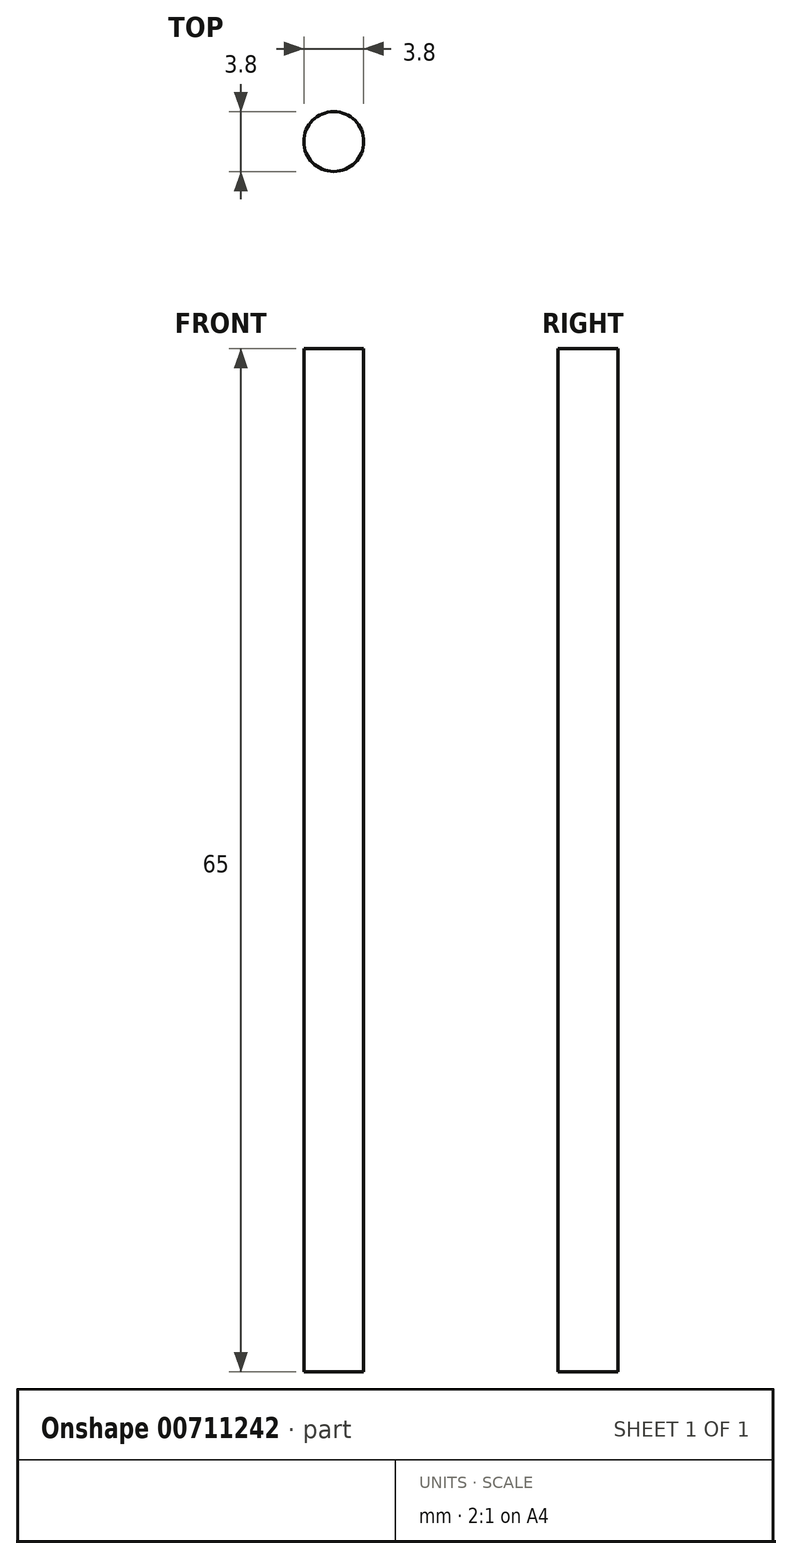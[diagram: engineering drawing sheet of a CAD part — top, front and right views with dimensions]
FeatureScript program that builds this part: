
annotation { "Feature Type Name" : "Feature", "Feature Type Description" : "" }
export const myFeature = defineFeature(function(context is Context, id is Id, definition is map)
    precondition{}
    {
        {
            var Q0;
            Q0=qCreatedBy(makeId("Top.planeOp"),FACE);
            var sketch = newSketch(context, id + "F0", { "sketchPlane" : qUnion([Q0])});
            skCircle(sketch, "E0", {"center": v(0, 0) * mm, "radius": 1.9 * mm});
            skSolve(sketch);
        }
        {
            var Q0;
            Q0=makeQuery(id+"F0.imprint","IMPRINT",FACE,{"disambiguationData":[TD([[makeQuery(id+"F0.imprint","IMPRINT",EDGE,{"derivedFrom":sQuery(id+"F0.wireOp",EDGE,"E0")}),1.0]])]});
            extrude(context, id + "F1", {"entities" : qUnion([Q0]), "depth" : 65 * mm, "offsetDistance" : 25 * mm});
        }
    });
